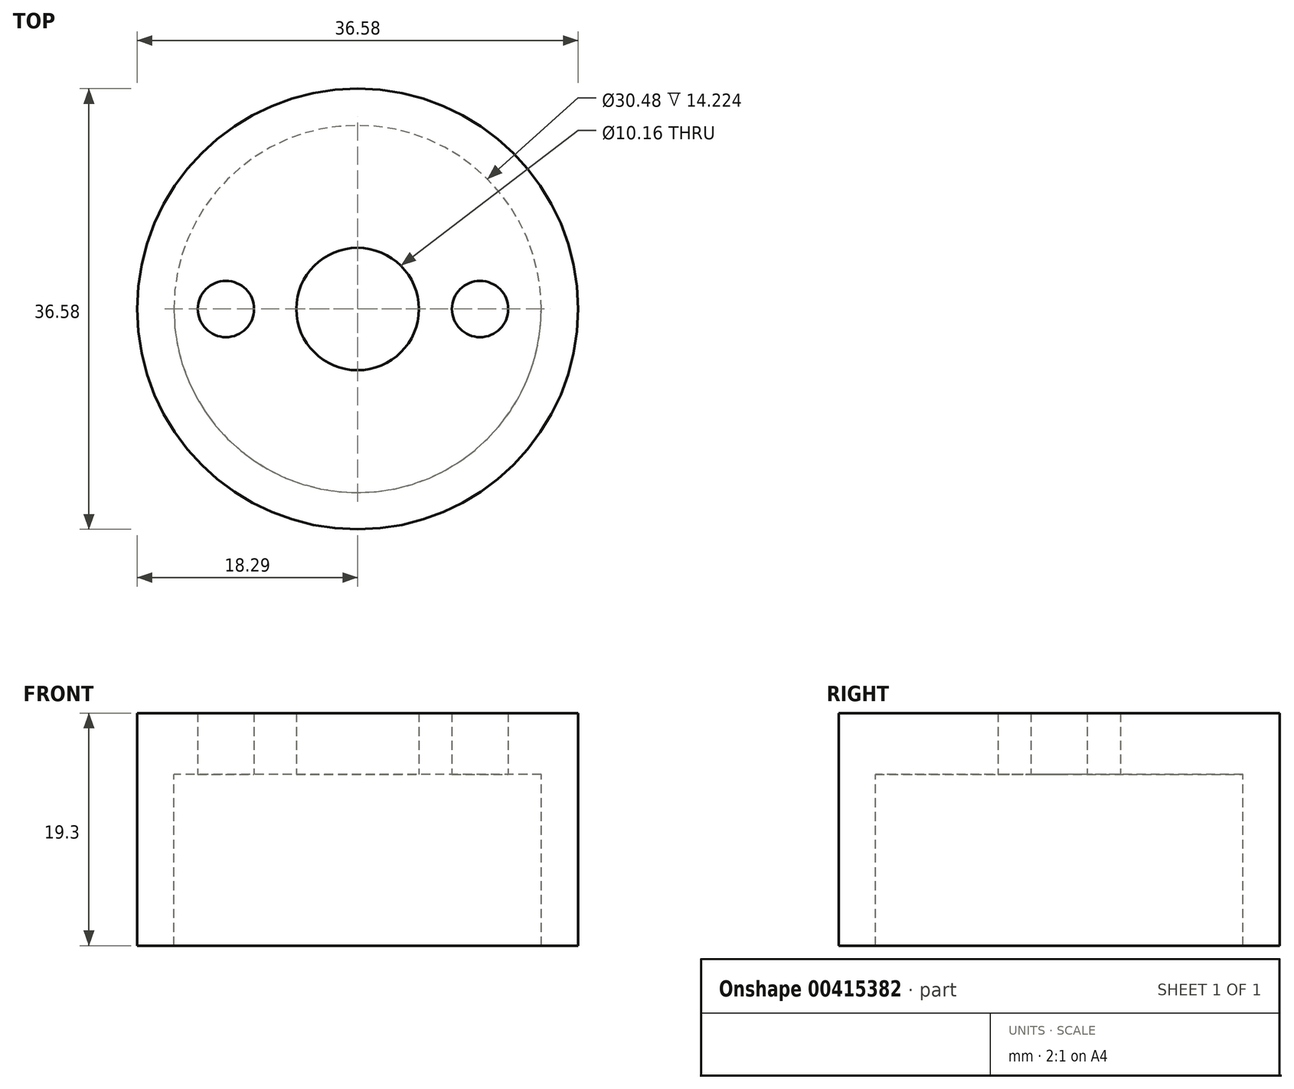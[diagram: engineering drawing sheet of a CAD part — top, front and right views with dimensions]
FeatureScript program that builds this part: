
annotation { "Feature Type Name" : "Feature", "Feature Type Description" : "" }
export const myFeature = defineFeature(function(context is Context, id is Id, definition is map)
    precondition{}
    {
        {
            var Q0;
            Q0=qCreatedBy(makeId("Front.planeOp"),FACE);
            var sketch = newSketch(context, id + "F0", { "sketchPlane" : qUnion([Q0])});
            skLineSegment(sketch, "E0.bottom", {"start": v(-18.29, 5.08) * mm, "end": v(0, 5.08) * mm});
            skLineSegment(sketch, "E0.top", {"start": v(-18.29, -14.22) * mm, "end": v(0, -14.22) * mm});
            skLineSegment(sketch, "E0.left", {"start": v(-18.29, 5.08) * mm, "end": v(-18.29, -14.22) * mm});
            skLineSegment(sketch, "E0.right", {"start": v(0, 5.08) * mm, "end": v(0, -14.22) * mm});
            skSolve(sketch);
        }
        {
            var Q0;
            Q0=makeQuery(id+"F0.imprint","IMPRINT",FACE,{"disambiguationData":[TD([[makeQuery(id+"F0.imprint","IMPRINT",EDGE,{"derivedFrom":sQuery(id+"F0.wireOp",EDGE,"E0.bottom")}),-1.0]])]});
            var Q1;
            Q1=sQuery(id+"F0.wireOp",EDGE,"E0.right");
            revolve(context, id + "F1", {"entities" : qUnion([Q0]), "axis" : qUnion([Q1]), "revolveType" : RevolveType.FULL});
        }
        {
            var Q0;
            Q0=qCreatedBy(makeId("Top.planeOp"),FACE);
            var sketch = newSketch(context, id + "F2", { "sketchPlane" : qUnion([Q0])});
            skCircle(sketch, "E1", {"center": v(0, 0) * mm, "radius": 14.65 * mm});
            skSolve(sketch);
        }
        {
            var Q0;
            Q0=sQuery(id+"F2.wireOp",VERTEX,"E1.center");
            var Q1;
            Q1=makeQuery(id+"F1.opRevolve","SWEPT_BODY",BODY,{"disambiguationData":[OSD([sQuery(id+"F0.wireOp",EDGE,"E0.bottom"),sQuery(id+"F0.wireOp",EDGE,"E0.top"),sQuery(id+"F0.wireOp",EDGE,"E0.left"),sQuery(id+"F0.wireOp",EDGE,"E0.right")])]});
            hole(context, id + "F3", {"style" : HoleStyle.SIMPLE, "endStyle" : HoleEndStyle.BLIND, "holeDiameter" : 30.48 * mm, "holeDepth" : 16.5 * mm, "isTappedThrough" : true, "tappedDepth" : 12.7 * mm, "tapClearance" : 3, "startFromSketch" : true, "locations" : qUnion([Q0]), "scope" : qUnion([Q1])});
        }
        {
            var Q0;
            Q0=qCreatedBy(makeId("Top.planeOp"),FACE);
            var sketch = newSketch(context, id + "F4", { "sketchPlane" : qUnion([Q0])});
            skCircle(sketch, "E2", {"center": v(0, 0) * mm, "radius": 5.18 * mm});
            skSolve(sketch);
        }
        {
            var Q0;
            Q0=sQuery(id+"F4.wireOp",VERTEX,"E2.center");
            var Q1;
            Q1=makeQuery(id+"F1.opRevolve","SWEPT_BODY",BODY,{"disambiguationData":[OSD([sQuery(id+"F0.wireOp",EDGE,"E0.bottom"),sQuery(id+"F0.wireOp",EDGE,"E0.top"),sQuery(id+"F0.wireOp",EDGE,"E0.left"),sQuery(id+"F0.wireOp",EDGE,"E0.right")])]});
            hole(context, id + "F5", {"style" : HoleStyle.SIMPLE, "endStyle" : HoleEndStyle.THROUGH, "oppositeDirection" : true, "holeDiameter" : 10.16 * mm, "isTappedThrough" : true, "tappedDepth" : 12.7 * mm, "tapClearance" : 3, "startFromSketch" : true, "locations" : qUnion([Q0]), "scope" : qUnion([Q1])});
        }
        {
            var Q0;
            Q0=qCreatedBy(makeId("Top.planeOp"),FACE);
            var sketch = newSketch(context, id + "F6", { "sketchPlane" : qUnion([Q0])});
            skCircle(sketch, "E3", {"center": v(-10.92, 0) * mm, "radius": 2.34 * mm});
            skCircle(sketch, "E4", {"center": v(10.67, 0) * mm, "radius": 2.34 * mm});
            skSolve(sketch);
        }
        {
            var Q0;
            Q0=sQuery(id+"F6.wireOp",VERTEX,"E3.center");
            var Q1;
            Q1=makeQuery(id+"F1.opRevolve","SWEPT_BODY",BODY,{"disambiguationData":[OSD([sQuery(id+"F0.wireOp",EDGE,"E0.bottom"),sQuery(id+"F0.wireOp",EDGE,"E0.top"),sQuery(id+"F0.wireOp",EDGE,"E0.left"),sQuery(id+"F0.wireOp",EDGE,"E0.right")])]});
            hole(context, id + "F7", {"style" : HoleStyle.SIMPLE, "endStyle" : HoleEndStyle.THROUGH, "oppositeDirection" : true, "holeDiameter" : 4.67 * mm, "isTappedThrough" : true, "tappedDepth" : 12.7 * mm, "tapClearance" : 3, "startFromSketch" : true, "locations" : qUnion([Q0]), "scope" : qUnion([Q1])});
        }
        {
            var Q0;
            Q0=qCreatedBy(makeId("Top.planeOp"),FACE);
            var sketch = newSketch(context, id + "F8", { "sketchPlane" : qUnion([Q0])});
            skCircle(sketch, "E5", {"center": v(10.16, 0) * mm, "radius": 2.29 * mm});
            skSolve(sketch);
        }
        {
            var Q0;
            Q0=sQuery(id+"F8.wireOp",VERTEX,"E5.center");
            var Q1;
            Q1=makeQuery(id+"F1.opRevolve","SWEPT_BODY",BODY,{"disambiguationData":[OSD([sQuery(id+"F0.wireOp",EDGE,"E0.bottom"),sQuery(id+"F0.wireOp",EDGE,"E0.top"),sQuery(id+"F0.wireOp",EDGE,"E0.left"),sQuery(id+"F0.wireOp",EDGE,"E0.right")])]});
            hole(context, id + "F9", {"style" : HoleStyle.SIMPLE, "endStyle" : HoleEndStyle.THROUGH, "oppositeDirection" : true, "holeDiameter" : 4.67 * mm, "isTappedThrough" : true, "tappedDepth" : 12.7 * mm, "tapClearance" : 3, "startFromSketch" : true, "locations" : qUnion([Q0]), "scope" : qUnion([Q1])});
        }
    });
